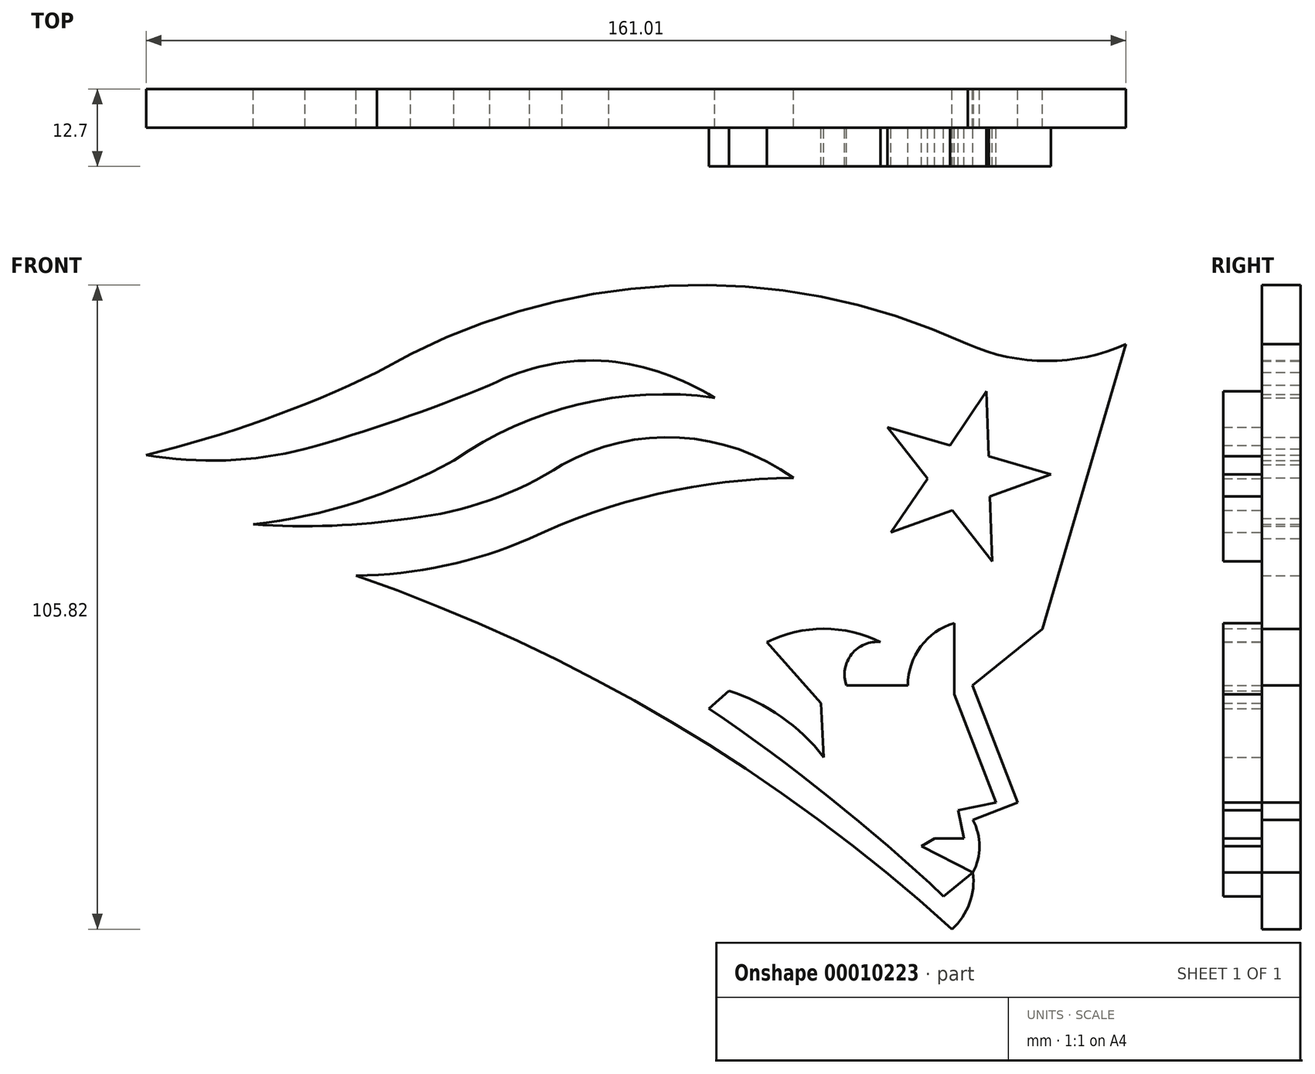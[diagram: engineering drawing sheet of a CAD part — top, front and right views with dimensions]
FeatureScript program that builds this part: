
annotation { "Feature Type Name" : "Feature", "Feature Type Description" : "" }
export const myFeature = defineFeature(function(context is Context, id is Id, definition is map)
    precondition{}
    {
        {
            var Q0;
            Q0=qCreatedBy(makeId("Front.planeOp"),FACE);
            var sketch = newSketch(context, id + "F0", { "sketchPlane" : qUnion([Q0])});
            skLineSegment(sketch, "E0", {"start": v(29.54, 58.43) * mm, "end": v(15.81, 11.69) * mm});
            skLineSegment(sketch, "E1", {"start": v(15.81, 11.69) * mm, "end": v(4.31, 2.41) * mm});
            skLineSegment(sketch, "E2", {"start": v(4.31, 2.41) * mm, "end": v(11.73, -16.88) * mm});
            skLineSegment(sketch, "E3", {"start": v(11.73, -16.88) * mm, "end": v(4.4, -19.7) * mm});
            skArc(sketch, "E4", {"start": v(4.4, -28.38) * mm, "mid": v(5.44, -24.04) * mm, "end": v(4.4, -19.7) * mm});
            skArc(sketch, "E5", {"start": v(0.97, -37.66) * mm, "mid": v(3.82, -33.44) * mm, "end": v(4.4, -28.38) * mm});
            skArc(sketch, "E6", {"start": v(3.57, 58.43) * mm, "mid": v(16.55, 55.7) * mm, "end": v(29.54, 58.43) * mm});
            skLineSegment(sketch, "E7", {"start": v(3.57, 58.43) * mm, "end": v(3.57, 58.43) * mm});
            skArc(sketch, "E8", {"start": v(-88, 29.84) * mm, "mid": v(-75.04, 32.8) * mm, "end": v(-63.12, 38.63) * mm});
            skArc(sketch, "E9", {"start": v(-113.86, 28.84) * mm, "mid": v(-100.9, 28.64) * mm, "end": v(-88, 29.84) * mm});
            skArc(sketch, "E10", {"start": v(-113.86, 28.84) * mm, "mid": v(-96.86, 32.47) * mm, "end": v(-80.88, 39.33) * mm});
            skArc(sketch, "E11", {"start": v(-38.05, 49.66) * mm, "mid": v(-60.44, 48.54) * mm, "end": v(-80.88, 39.33) * mm});
            skArc(sketch, "E12", {"start": v(-25.1, 36.46) * mm, "mid": v(-43.8, 43.1) * mm, "end": v(-63.12, 38.63) * mm});
            skArc(sketch, "E13", {"start": v(-131.47, 40.25) * mm, "mid": v(-112.15, 46) * mm, "end": v(-93.55, 53.8) * mm});
            skArc(sketch, "E14", {"start": v(3.57, 58.43) * mm, "mid": v(-45.56, 68.04) * mm, "end": v(-93.55, 53.8) * mm});
            skArc(sketch, "E15", {"start": v(-131.47, 40.25) * mm, "mid": v(-118.36, 39.37) * mm, "end": v(-105.35, 41.23) * mm});
            skArc(sketch, "E16", {"start": v(-38.05, 49.66) * mm, "mid": v(-46.42, 53.62) * mm, "end": v(-55.45, 55.66) * mm});
            skPoint(sketch, "E17.visualSharp", {"position": v(-67.17, 55.3) * mm});
            skArc(sketch, "E17.filletArc", {"start": v(-66.32, 55.44) * mm, "mid": v(-67.12, 55.26) * mm, "end": v(-67.9, 54.97) * mm});
            skArc(sketch, "E18", {"start": v(-105.35, 41.23) * mm, "mid": v(-90.02, 46.03) * mm, "end": v(-75, 51.7) * mm});
            skArc(sketch, "E19", {"start": v(-96.94, 20.41) * mm, "mid": v(-82.4, 22.04) * mm, "end": v(-68.47, 26.51) * mm});
            skArc(sketch, "E20", {"start": v(-25.1, 36.46) * mm, "mid": v(-47.33, 33.86) * mm, "end": v(-68.47, 26.51) * mm});
            skArc(sketch, "E21", {"start": v(0.97, -37.66) * mm, "mid": v(-45.06, -3.69) * mm, "end": v(-96.94, 20.41) * mm});
            skArc(sketch, "E22", {"start": v(-55.45, 55.66) * mm, "mid": v(-65.5, 55.04) * mm, "end": v(-75, 51.7) * mm});
            skSolve(sketch);
        }
        {
            var Q0;
            Q0=makeQuery(id+"F0.imprint","IMPRINT",FACE,{"disambiguationData":[TD([[makeQuery(id+"F0.imprint","IMPRINT",EDGE,{"derivedFrom":sQuery(id+"F0.wireOp",EDGE,"E0")}),-1.0]])]});
            extrude(context, id + "F1", {"entities" : qUnion([Q0]), "depth" : 6.35 * mm});
        }
        {
            var Q0;
            Q0=makeQuery(id+"F1.opExtrude","CAP_FACE",FACE,{"disambiguationData":[OSD([sQuery(id+"F0.wireOp",EDGE,"E0"),sQuery(id+"F0.wireOp",EDGE,"E1"),sQuery(id+"F0.wireOp",EDGE,"E2"),sQuery(id+"F0.wireOp",EDGE,"E3"),sQuery(id+"F0.wireOp",EDGE,"E4"),sQuery(id+"F0.wireOp",EDGE,"E5"),sQuery(id+"F0.wireOp",EDGE,"E6"),sQuery(id+"F0.wireOp",EDGE,"5a7b0ea9-7add-4295-b359-09b799b26604"),sQuery(id+"F0.wireOp",EDGE,"a772a3d0-a05f-469f-ac4a-95de44ba73e0"),sQuery(id+"F0.wireOp",EDGE,"E7"),sQuery(id+"F0.wireOp",EDGE,"4a6b9d04-7878-4ad2-be5b-53405a07bcb8"),sQuery(id+"F0.wireOp",EDGE,"174b4cb9-bad4-48d5-bccc-986990c096a6"),sQuery(id+"F0.wireOp",EDGE,"bac64411-df81-4d94-83e7-b5dda78b5204"),sQuery(id+"F0.wireOp",EDGE,"cdebb211-51cd-4c1b-a1cf-e8e0b51789ba")])],"isStart":false});
            var sketch = newSketch(context, id + "F2", { "sketchPlane" : qUnion([Q0])});
            skArc(sketch, "E23", {"start": v(1.33, 12.6) * mm, "mid": v(-4.19, 8.78) * mm, "end": v(-6.3, 2.41) * mm});
            skLineSegment(sketch, "E24", {"start": v(-6.3, 2.41) * mm, "end": v(-16.42, 2.41) * mm});
            skArc(sketch, "E25", {"start": v(-10.79, 9.52) * mm, "mid": v(-15.54, 7.5) * mm, "end": v(-16.42, 2.41) * mm});
            skArc(sketch, "E26", {"start": v(-10.79, 9.52) * mm, "mid": v(-20.12, 11.7) * mm, "end": v(-29.45, 9.52) * mm});
            skLineSegment(sketch, "E27", {"start": v(-29.45, 9.52) * mm, "end": v(-20.57, -0.56) * mm});
            skLineSegment(sketch, "E28", {"start": v(-20.57, -0.56) * mm, "end": v(-20.12, -9.4) * mm});
            skArc(sketch, "E29", {"start": v(-20.12, -9.4) * mm, "mid": v(-27.09, -2.78) * mm, "end": v(-35.68, 1.52) * mm});
            skLineSegment(sketch, "E30", {"start": v(-35.68, 1.52) * mm, "end": v(-38.98, -1.4) * mm});
            skArc(sketch, "E31", {"start": v(-0.42, -32.26) * mm, "mid": v(-19.11, -16.1) * mm, "end": v(-38.98, -1.4) * mm});
            skLineSegment(sketch, "E32", {"start": v(8.17, -16.88) * mm, "end": v(1.97, -18.12) * mm});
            skLineSegment(sketch, "E33", {"start": v(1.97, -18.12) * mm, "end": v(2.9, -22.77) * mm});
            skLineSegment(sketch, "E34", {"start": v(2.9, -22.77) * mm, "end": v(-1.9, -22.77) * mm});
            skLineSegment(sketch, "E35", {"start": v(-1.9, -22.77) * mm, "end": v(-4.07, -24.04) * mm});
            skLineSegment(sketch, "E36", {"start": v(-4.07, -24.04) * mm, "end": v(4.4, -28.38) * mm});
            skLineSegment(sketch, "E37", {"start": v(4.4, -28.38) * mm, "end": v(-0.42, -32.26) * mm});
            skLineSegment(sketch, "E38", {"start": v(8.17, -16.88) * mm, "end": v(1.33, 0.9) * mm});
            skLineSegment(sketch, "E39", {"start": v(1.33, 0.9) * mm, "end": v(1.33, 12.6) * mm});
            skCircle(sketch, "E40.cCircle", {"center": v(2.54, 36.56) * mm, "radius": 4.54 * mm, "construction": true});
            skLineSegment(sketch, "E40.0", {"start": v(-3.07, 36.38) * mm, "end": v(0.63, 41.85) * mm});
            skLineSegment(sketch, "E40.1", {"start": v(0.63, 41.85) * mm, "end": v(6.97, 40.02) * mm});
            skLineSegment(sketch, "E40.2", {"start": v(6.97, 40.02) * mm, "end": v(7.2, 33.42) * mm});
            skLineSegment(sketch, "E40.3", {"start": v(7.2, 33.42) * mm, "end": v(0.98, 31.17) * mm});
            skLineSegment(sketch, "E40.4", {"start": v(0.98, 31.17) * mm, "end": v(-3.07, 36.38) * mm});
            skPoint(sketch, "E40.0.midPoint", {"position": v(-1.22, 39.11) * mm});
            skLineSegment(sketch, "E41", {"start": v(7.2, 33.42) * mm, "end": v(7.55, 22.74) * mm});
            skLineSegment(sketch, "E42", {"start": v(7.55, 22.74) * mm, "end": v(0.98, 31.17) * mm});
            skLineSegment(sketch, "E43", {"start": v(0.98, 31.17) * mm, "end": v(-9.06, 27.53) * mm});
            skLineSegment(sketch, "E44", {"start": v(-9.06, 27.53) * mm, "end": v(-3.07, 36.38) * mm});
            skLineSegment(sketch, "E45", {"start": v(-3.07, 36.38) * mm, "end": v(-9.64, 44.8) * mm});
            skLineSegment(sketch, "E46", {"start": v(-9.64, 44.8) * mm, "end": v(0.63, 41.85) * mm});
            skLineSegment(sketch, "E47", {"start": v(6.97, 40.02) * mm, "end": v(17.23, 37.06) * mm});
            skLineSegment(sketch, "E48", {"start": v(17.23, 37.06) * mm, "end": v(7.2, 33.42) * mm});
            skLineSegment(sketch, "E49", {"start": v(6.97, 40.02) * mm, "end": v(6.61, 50.7) * mm});
            skLineSegment(sketch, "E50", {"start": v(6.61, 50.7) * mm, "end": v(0.63, 41.85) * mm});
            skSolve(sketch);
        }
        {
            var Q0;
            Q0=makeQuery(id+"F2.imprint","IMPRINT",FACE,{"disambiguationData":[TD([[makeQuery(id+"F2.imprint","IMPRINT",EDGE,{"derivedFrom":sQuery(id+"F2.wireOp",EDGE,"f87b9d5e-e48a-4e62-b66d-5e8aaa541502")}),-1.0]])]});
            var Q1;
            Q1=makeQuery(id+"F2.imprint","IMPRINT",FACE,{"disambiguationData":[TD([[makeQuery(id+"F2.imprint","IMPRINT",EDGE,{"derivedFrom":sQuery(id+"F2.wireOp",EDGE,"E23")}),1.0]])]});
            extrude(context, id + "F3", {"entities" : qUnion([Q0, Q1]), "operationType" : NewBodyOperationType.ADD, "depth" : 6.35 * mm});
        }
        {
            var Q0;
            Q0 = qSketchRegion(id + "F2", true);
            extrude(context, id + "F4", {"entities" : qUnion([Q0]), "operationType" : NewBodyOperationType.ADD, "depth" : 6.35 * mm});
        }
    });
